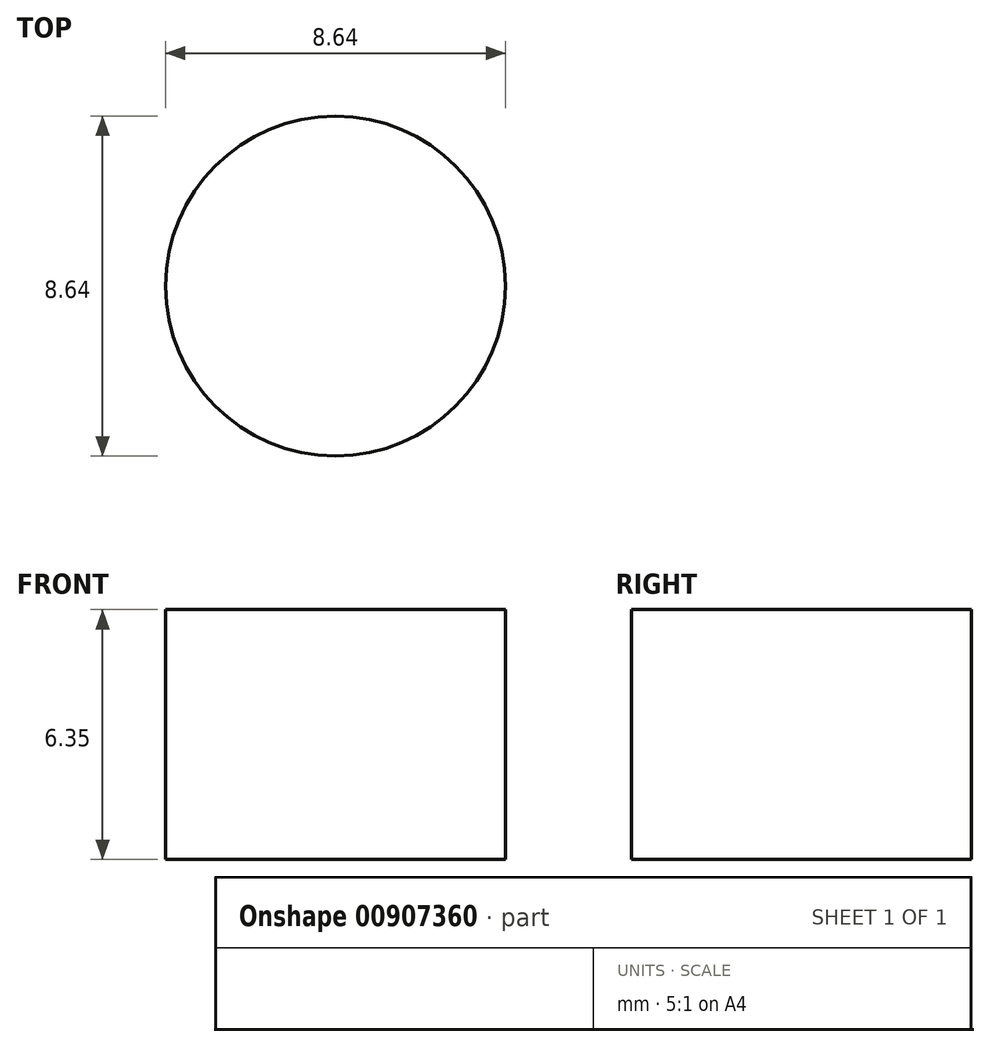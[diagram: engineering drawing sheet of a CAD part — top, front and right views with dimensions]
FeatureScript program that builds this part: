
annotation { "Feature Type Name" : "Feature", "Feature Type Description" : "" }
export const myFeature = defineFeature(function(context is Context, id is Id, definition is map)
    precondition{}
    {
        {
            var Q0;
            Q0=qCreatedBy(makeId("Top.planeOp"),FACE);
            var sketch = newSketch(context, id + "F0", { "sketchPlane" : qUnion([Q0])});
            skCircle(sketch, "E0", {"center": v(0, 0) * mm, "radius": 4.32 * mm});
            skSolve(sketch);
        }
        {
            var Q0;
            Q0 = qSketchRegion(id + "F0", true);
            extrude(context, id + "F1", {"entities" : qUnion([Q0]), "depth" : 6.35 * mm, "offsetDistance" : 25.4 * mm});
        }
    });
